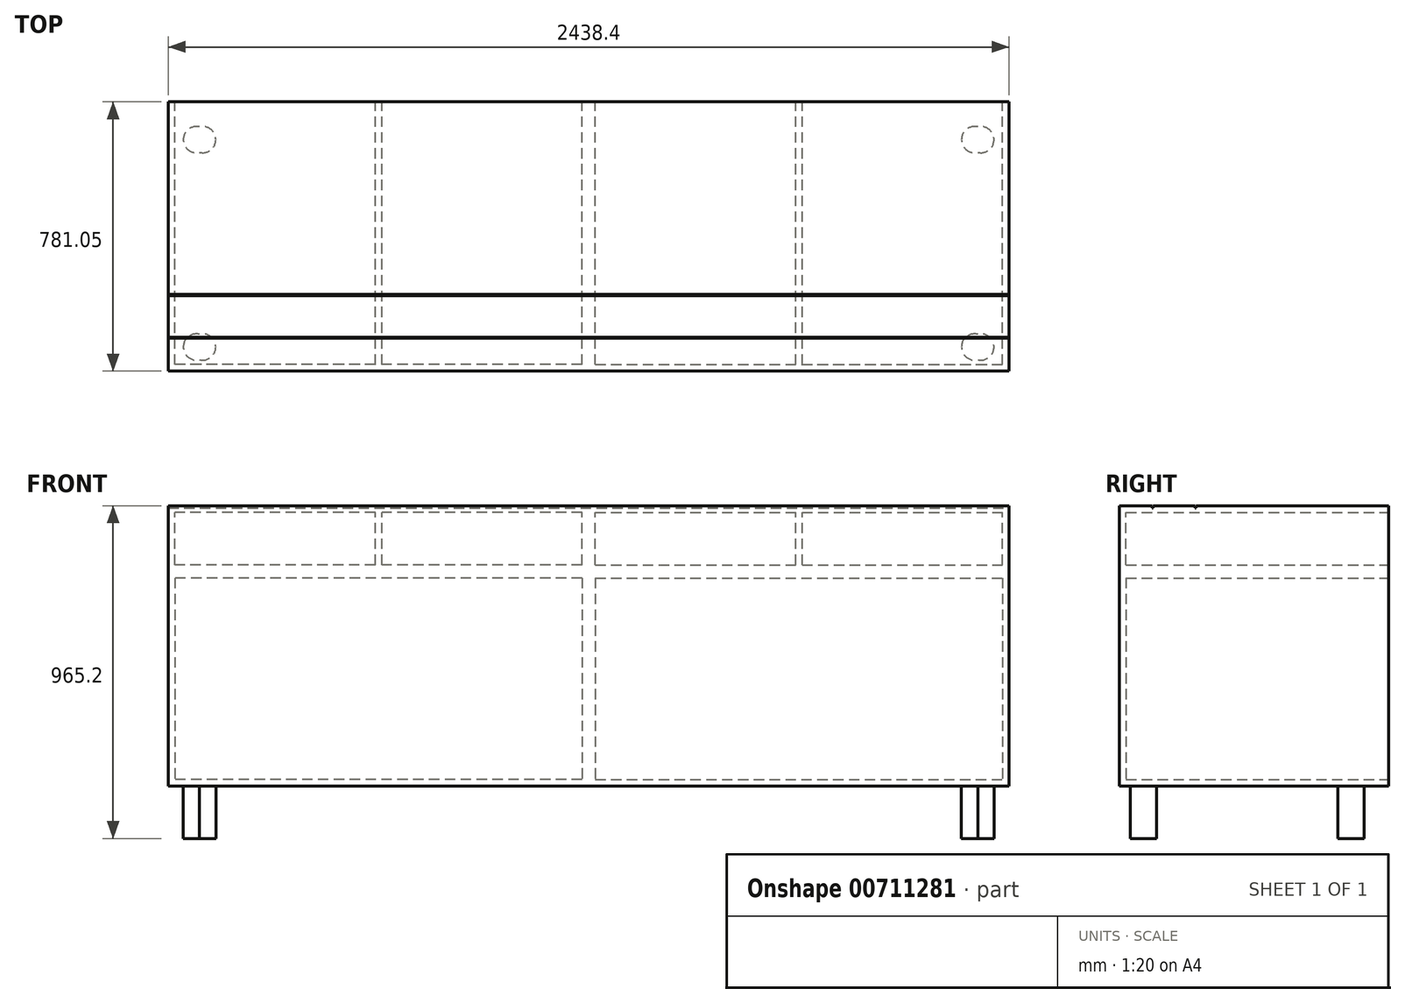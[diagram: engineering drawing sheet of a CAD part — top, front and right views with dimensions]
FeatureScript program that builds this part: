
annotation { "Feature Type Name" : "Feature", "Feature Type Description" : "" }
export const myFeature = defineFeature(function(context is Context, id is Id, definition is map)
    precondition{}
    {
        {
            var Q0;
            Q0=qCreatedBy(makeId("Front.planeOp"),FACE);
            var sketch = newSketch(context, id + "F0", { "sketchPlane" : qUnion([Q0])});
            skLineSegment(sketch, "E0.bottom", {"start": v(0, 0) * mm, "end": v(-1219.2, 0) * mm});
            skLineSegment(sketch, "E0.top", {"start": v(0, 190.5) * mm, "end": v(-1219.2, 190.5) * mm});
            skLineSegment(sketch, "E0.left", {"start": v(0, 0) * mm, "end": v(0, 190.5) * mm});
            skLineSegment(sketch, "E0.right", {"start": v(-1219.2, 0) * mm, "end": v(-1219.2, 190.5) * mm});
            skLineSegment(sketch, "E1.0", {"start": v(-19.05, 171.45) * mm, "end": v(-1200.15, 171.45) * mm});
            skLineSegment(sketch, "E1.1", {"start": v(-19.05, 19.05) * mm, "end": v(-19.05, 171.45) * mm});
            skLineSegment(sketch, "E1.2", {"start": v(-19.05, 19.05) * mm, "end": v(-1200.15, 19.05) * mm});
            skLineSegment(sketch, "E1.3", {"start": v(-1200.15, 19.05) * mm, "end": v(-1200.15, 171.45) * mm});
            skSolve(sketch);
        }
        {
            var Q0;
            Q0 = qSketchRegion(id + "F0", true);
            extrude(context, id + "F1", {"entities" : qUnion([Q0]), "depth" : 762 * mm, "offsetDistance" : 25.4 * mm});
        }
        {
            var Q0;
            Q0=qCreatedBy(makeId("Front.planeOp"),FACE);
            var sketch = newSketch(context, id + "F2", { "sketchPlane" : qUnion([Q0])});
            skLineSegment(sketch, "E2.bottom", {"start": v(0, 0) * mm, "end": v(1219.2, 0) * mm});
            skLineSegment(sketch, "E2.top", {"start": v(0, 190.5) * mm, "end": v(1219.2, 190.5) * mm});
            skLineSegment(sketch, "E2.left", {"start": v(0, 0) * mm, "end": v(0, 190.5) * mm});
            skLineSegment(sketch, "E2.right", {"start": v(1219.2, 0) * mm, "end": v(1219.2, 190.5) * mm});
            skLineSegment(sketch, "E3.0", {"start": v(19.05, 171.45) * mm, "end": v(1200.15, 171.45) * mm});
            skLineSegment(sketch, "E3.1", {"start": v(19.05, 19.05) * mm, "end": v(19.05, 171.45) * mm});
            skLineSegment(sketch, "E3.2", {"start": v(19.05, 19.05) * mm, "end": v(1200.15, 19.05) * mm});
            skLineSegment(sketch, "E3.3", {"start": v(1200.15, 19.05) * mm, "end": v(1200.15, 171.45) * mm});
            skSolve(sketch);
        }
        {
            var Q0;
            Q0=makeQuery(id+"F2.imprint","IMPRINT",FACE,{"disambiguationData":[TD([[makeQuery(id+"F2.imprint","IMPRINT",EDGE,{"derivedFrom":sQuery(id+"F2.wireOp",EDGE,"E2.bottom")}),1.0]])]});
            extrude(context, id + "F3", {"entities" : qUnion([Q0]), "operationType" : NewBodyOperationType.ADD, "depth" : 762 * mm, "offsetDistance" : 25.4 * mm});
        }
        {
            var Q0;
            Q0=qCreatedBy(makeId("Front.planeOp"),FACE);
            var sketch = newSketch(context, id + "F4", { "sketchPlane" : qUnion([Q0])});
            skLineSegment(sketch, "E4.bottom", {"start": v(0, 0) * mm, "end": v(-1219.2, 0) * mm});
            skLineSegment(sketch, "E4.top", {"start": v(0, -622.3) * mm, "end": v(-1219.2, -622.3) * mm});
            skLineSegment(sketch, "E4.left", {"start": v(0, 0) * mm, "end": v(0, -622.3) * mm});
            skLineSegment(sketch, "E4.right", {"start": v(-1219.2, 0) * mm, "end": v(-1219.2, -622.3) * mm});
            skLineSegment(sketch, "E5.0", {"start": v(-19.05, -603.25) * mm, "end": v(-1200.15, -603.25) * mm});
            skLineSegment(sketch, "E5.1", {"start": v(-19.05, -19.05) * mm, "end": v(-19.05, -603.25) * mm});
            skLineSegment(sketch, "E5.2", {"start": v(-19.05, -19.05) * mm, "end": v(-1200.15, -19.05) * mm});
            skLineSegment(sketch, "E5.3", {"start": v(-1200.15, -19.05) * mm, "end": v(-1200.15, -603.25) * mm});
            skLineSegment(sketch, "E6.0", {"start": v(1219.2, 190.5) * mm, "end": v(-1219.2, 190.5) * mm});
            skSolve(sketch);
        }
        {
            var Q0;
            Q0=makeQuery(id+"F4.imprint","IMPRINT",FACE,{"disambiguationData":[TD([[makeQuery(id+"F4.imprint","IMPRINT",EDGE,{"derivedFrom":sQuery(id+"F4.wireOp",EDGE,"E4.bottom")}),1.0]])]});
            extrude(context, id + "F5", {"entities" : qUnion([Q0]), "operationType" : NewBodyOperationType.ADD, "depth" : 762 * mm, "offsetDistance" : 25.4 * mm});
        }
        {
            var Q0;
            Q0=qCreatedBy(makeId("Front.planeOp"),FACE);
            var sketch = newSketch(context, id + "F6", { "sketchPlane" : qUnion([Q0])});
            skLineSegment(sketch, "E7.bottom", {"start": v(0, 0) * mm, "end": v(1219.2, 0) * mm});
            skLineSegment(sketch, "E7.top", {"start": v(0, -622.3) * mm, "end": v(1219.2, -622.3) * mm});
            skLineSegment(sketch, "E7.left", {"start": v(0, 0) * mm, "end": v(0, -622.3) * mm});
            skLineSegment(sketch, "E7.right", {"start": v(1219.2, 0) * mm, "end": v(1219.2, -622.3) * mm});
            skLineSegment(sketch, "E8.0", {"start": v(1219.2, 190.5) * mm, "end": v(-1219.2, 190.5) * mm});
            skLineSegment(sketch, "E9.0", {"start": v(1200.15, -19.05) * mm, "end": v(1200.15, -603.25) * mm});
            skLineSegment(sketch, "E9.1", {"start": v(19.05, -19.05) * mm, "end": v(1200.15, -19.05) * mm});
            skLineSegment(sketch, "E9.2", {"start": v(19.05, -19.05) * mm, "end": v(19.05, -603.25) * mm});
            skLineSegment(sketch, "E9.3", {"start": v(19.05, -603.25) * mm, "end": v(1200.15, -603.25) * mm});
            skSolve(sketch);
        }
        {
            var Q0;
            Q0=makeQuery(id+"F6.imprint","IMPRINT",FACE,{"disambiguationData":[TD([[makeQuery(id+"F6.imprint","IMPRINT",EDGE,{"derivedFrom":sQuery(id+"F6.wireOp",EDGE,"E7.bottom")}),-1.0]])]});
            extrude(context, id + "F7", {"entities" : qUnion([Q0]), "operationType" : NewBodyOperationType.ADD, "depth" : 762 * mm, "offsetDistance" : 25.4 * mm});
        }
        {
            var Q0;
            Q0=makeQuery(id+"F3.boolean.opBoolean","MERGE",FACE,{"derivedFrom":[makeQuery(id+"F1.opExtrude","SWEPT_FACE",FACE,{"disambiguationData":[OSD([sQuery(id+"F0.wireOp",EDGE,"E0.top")])]}),makeQuery(id+"F3.opExtrude","SWEPT_FACE",FACE,{"disambiguationData":[OSD([sQuery(id+"F2.wireOp",EDGE,"E2.top")])]})]});
            var sketch = newSketch(context, id + "F8", { "sketchPlane" : qUnion([Q0])});
            skLineSegment(sketch, "E10.bottom", {"start": v(-1219.2, -685.8) * mm, "end": v(1219.2, -685.8) * mm});
            skLineSegment(sketch, "E10.top", {"start": v(-1219.2, -558.8) * mm, "end": v(1219.2, -558.8) * mm});
            skLineSegment(sketch, "E10.left", {"start": v(-1219.2, -685.8) * mm, "end": v(-1219.2, -558.8) * mm});
            skLineSegment(sketch, "E10.right", {"start": v(1219.2, -685.8) * mm, "end": v(1219.2, -558.8) * mm});
            skSolve(sketch);
        }
        {
            var Q0;
            Q0=makeQuery(id+"F8.imprint","IMPRINT",FACE,{"disambiguationData":[TD([[makeQuery(id+"F8.imprint","IMPRINT",EDGE,{"derivedFrom":sQuery(id+"F8.wireOp",EDGE,"E10.bottom")}),1.0]])]});
            extrude(context, id + "F9", {"entities" : qUnion([Q0]), "operationType" : NewBodyOperationType.REMOVE, "oppositeDirection" : true, "depth" : 6.35 * mm, "offsetDistance" : 25.4 * mm});
        }
        {
            var Q0;
            Q0=makeQuery(id+"F7.boolean.opBoolean","MERGE",FACE,{"derivedFrom":[makeQuery(id+"F5.boolean.opBoolean","MERGE",FACE,{"derivedFrom":[makeQuery(id+"F3.boolean.opBoolean","MERGE",FACE,{"derivedFrom":[makeQuery(id+"F1.opExtrude","CAP_FACE",FACE,{"disambiguationData":[OSD([sQuery(id+"F0.wireOp",EDGE,"E0.bottom"),sQuery(id+"F0.wireOp",EDGE,"E0.top"),sQuery(id+"F0.wireOp",EDGE,"E0.left"),sQuery(id+"F0.wireOp",EDGE,"E0.right"),sQuery(id+"F0.wireOp",EDGE,"E1.0"),sQuery(id+"F0.wireOp",EDGE,"E1.1"),sQuery(id+"F0.wireOp",EDGE,"E1.2"),sQuery(id+"F0.wireOp",EDGE,"E1.3")])],"isStart":false}),makeQuery(id+"F3.opExtrude","CAP_FACE",FACE,{"disambiguationData":[OSD([sQuery(id+"F2.wireOp",EDGE,"E2.bottom"),sQuery(id+"F2.wireOp",EDGE,"E2.top"),sQuery(id+"F2.wireOp",EDGE,"E2.left"),sQuery(id+"F2.wireOp",EDGE,"E2.right"),sQuery(id+"F2.wireOp",EDGE,"E3.0"),sQuery(id+"F2.wireOp",EDGE,"E3.1"),sQuery(id+"F2.wireOp",EDGE,"E3.2"),sQuery(id+"F2.wireOp",EDGE,"E3.3")])],"isStart":false})]}),makeQuery(id+"F5.opExtrude","CAP_FACE",FACE,{"disambiguationData":[OSD([sQuery(id+"F4.wireOp",EDGE,"E4.bottom"),sQuery(id+"F4.wireOp",EDGE,"E4.top"),sQuery(id+"F4.wireOp",EDGE,"E4.left"),sQuery(id+"F4.wireOp",EDGE,"E4.right"),sQuery(id+"F4.wireOp",EDGE,"E5.0"),sQuery(id+"F4.wireOp",EDGE,"E5.1"),sQuery(id+"F4.wireOp",EDGE,"E5.2"),sQuery(id+"F4.wireOp",EDGE,"E5.3")])],"isStart":false})]}),makeQuery(id+"F7.opExtrude","CAP_FACE",FACE,{"disambiguationData":[OSD([sQuery(id+"F6.wireOp",EDGE,"E7.bottom"),sQuery(id+"F6.wireOp",EDGE,"E7.top"),sQuery(id+"F6.wireOp",EDGE,"E7.left"),sQuery(id+"F6.wireOp",EDGE,"E7.right"),sQuery(id+"F6.wireOp",EDGE,"E9.0"),sQuery(id+"F6.wireOp",EDGE,"E9.1"),sQuery(id+"F6.wireOp",EDGE,"E9.2"),sQuery(id+"F6.wireOp",EDGE,"E9.3")])],"isStart":false})]});
            var sketch = newSketch(context, id + "F10", { "sketchPlane" : qUnion([Q0])});
            skLineSegment(sketch, "E11.bottom", {"start": v(-1219.2, -622.3) * mm, "end": v(1219.2, -622.3) * mm});
            skLineSegment(sketch, "E11.top", {"start": v(-1219.2, 190.5) * mm, "end": v(1219.2, 190.5) * mm});
            skLineSegment(sketch, "E11.left", {"start": v(-1219.2, -622.3) * mm, "end": v(-1219.2, 190.5) * mm});
            skLineSegment(sketch, "E11.right", {"start": v(1219.2, -622.3) * mm, "end": v(1219.2, 190.5) * mm});
            skSolve(sketch);
        }
        {
            var Q0;
            Q0 = qSketchRegion(id + "F10", true);
            extrude(context, id + "F11", {"entities" : qUnion([Q0]), "operationType" : NewBodyOperationType.ADD, "depth" : 19.05 * mm, "offsetDistance" : 25.4 * mm});
        }
        {
            var Q0;
            Q0=makeQuery(id+"F11.boolean.opBoolean","MERGE",FACE,{"derivedFrom":[makeQuery(id+"F7.boolean.opBoolean","MERGE",FACE,{"derivedFrom":[makeQuery(id+"F5.opExtrude","SWEPT_FACE",FACE,{"disambiguationData":[OSD([sQuery(id+"F4.wireOp",EDGE,"E4.top")])]}),makeQuery(id+"F7.opExtrude","SWEPT_FACE",FACE,{"disambiguationData":[OSD([sQuery(id+"F6.wireOp",EDGE,"E7.top")])]})]}),makeQuery(id+"F11.opExtrude","SWEPT_FACE",FACE,{"disambiguationData":[OSD([sQuery(id+"F10.wireOp",EDGE,"E11.bottom")])]})]});
            var sketch = newSketch(context, id + "F12", { "sketchPlane" : qUnion([Q0])});
            skCircle(sketch, "E12", {"center": v(1119.46, 109.38) * mm, "radius": 38.1 * mm});
            skLineSegment(sketch, "E13.bottom", {"start": v(1119.46, 109.38) * mm, "end": v(-1137.54, 109.38) * mm, "construction": true});
            skLineSegment(sketch, "E13.top", {"start": v(1119.46, 710.9) * mm, "end": v(-1137.54, 710.9) * mm, "construction": true});
            skLineSegment(sketch, "E13.left", {"start": v(1119.46, 109.38) * mm, "end": v(1119.46, 710.9) * mm, "construction": true});
            skLineSegment(sketch, "E13.right", {"start": v(-1137.54, 109.38) * mm, "end": v(-1137.54, 710.9) * mm, "construction": true});
            skCircle(sketch, "E14", {"center": v(-1137.54, 710.9) * mm, "radius": 38.1 * mm});
            skCircle(sketch, "E15", {"center": v(1119.46, 710.9) * mm, "radius": 38.1 * mm});
            skCircle(sketch, "E16", {"center": v(-1137.54, 109.38) * mm, "radius": 38.1 * mm});
            skSolve(sketch);
        }
        {
            var Q0;
            Q0 = qSketchRegion(id + "F12", true);
            extrude(context, id + "F13", {"entities" : qUnion([Q0]), "operationType" : NewBodyOperationType.ADD, "depth" : 152.4 * mm, "offsetDistance" : 25.4 * mm});
        }
        {
            var Q0;
            Q0=makeQuery(id+"F7.boolean.opBoolean","MERGE",FACE,{"derivedFrom":[makeQuery(id+"F5.boolean.opBoolean","MERGE",FACE,{"derivedFrom":[makeQuery(id+"F3.boolean.opBoolean","MERGE",FACE,{"derivedFrom":[makeQuery(id+"F1.opExtrude","CAP_FACE",FACE,{"disambiguationData":[OSD([sQuery(id+"F0.wireOp",EDGE,"E0.bottom"),sQuery(id+"F0.wireOp",EDGE,"E0.top"),sQuery(id+"F0.wireOp",EDGE,"E0.left"),sQuery(id+"F0.wireOp",EDGE,"E0.right"),sQuery(id+"F0.wireOp",EDGE,"E1.0"),sQuery(id+"F0.wireOp",EDGE,"E1.1"),sQuery(id+"F0.wireOp",EDGE,"E1.2"),sQuery(id+"F0.wireOp",EDGE,"E1.3")])],"isStart":true}),makeQuery(id+"F3.opExtrude","CAP_FACE",FACE,{"disambiguationData":[OSD([sQuery(id+"F2.wireOp",EDGE,"E2.bottom"),sQuery(id+"F2.wireOp",EDGE,"E2.top"),sQuery(id+"F2.wireOp",EDGE,"E2.left"),sQuery(id+"F2.wireOp",EDGE,"E2.right"),sQuery(id+"F2.wireOp",EDGE,"E3.0"),sQuery(id+"F2.wireOp",EDGE,"E3.1"),sQuery(id+"F2.wireOp",EDGE,"E3.2"),sQuery(id+"F2.wireOp",EDGE,"E3.3")])],"isStart":true})]}),makeQuery(id+"F5.opExtrude","CAP_FACE",FACE,{"disambiguationData":[OSD([sQuery(id+"F4.wireOp",EDGE,"E4.bottom"),sQuery(id+"F4.wireOp",EDGE,"E4.top"),sQuery(id+"F4.wireOp",EDGE,"E4.left"),sQuery(id+"F4.wireOp",EDGE,"E4.right"),sQuery(id+"F4.wireOp",EDGE,"E5.0"),sQuery(id+"F4.wireOp",EDGE,"E5.1"),sQuery(id+"F4.wireOp",EDGE,"E5.2"),sQuery(id+"F4.wireOp",EDGE,"E5.3")])],"isStart":true})]}),makeQuery(id+"F7.opExtrude","CAP_FACE",FACE,{"disambiguationData":[OSD([sQuery(id+"F6.wireOp",EDGE,"E7.bottom"),sQuery(id+"F6.wireOp",EDGE,"E7.top"),sQuery(id+"F6.wireOp",EDGE,"E7.left"),sQuery(id+"F6.wireOp",EDGE,"E7.right"),sQuery(id+"F6.wireOp",EDGE,"E9.0"),sQuery(id+"F6.wireOp",EDGE,"E9.1"),sQuery(id+"F6.wireOp",EDGE,"E9.2"),sQuery(id+"F6.wireOp",EDGE,"E9.3")])],"isStart":true})]});
            var sketch = newSketch(context, id + "F14", { "sketchPlane" : qUnion([Q0])});
            skLineSegment(sketch, "E17.0", {"start": v(-19.05, 19.05) * mm, "end": v(-1200.15, 19.05) * mm, "construction": true});
            skLineSegment(sketch, "E17.1", {"start": v(-19.05, 171.45) * mm, "end": v(-1200.15, 171.45) * mm, "construction": true});
            skLineSegment(sketch, "E18.bottom", {"start": v(-600.07, 19.05) * mm, "end": v(-619.12, 19.05) * mm});
            skLineSegment(sketch, "E18.top", {"start": v(-600.07, 171.45) * mm, "end": v(-619.12, 171.45) * mm});
            skLineSegment(sketch, "E18.left", {"start": v(-600.07, 19.05) * mm, "end": v(-600.07, 171.45) * mm});
            skLineSegment(sketch, "E18.right", {"start": v(-619.12, 19.05) * mm, "end": v(-619.12, 171.45) * mm});
            skPoint(sketch, "E19", {"position": v(-609.6, 19.05) * mm});
            skSolve(sketch);
        }
        {
            var Q0;
            Q0 = qSketchRegion(id + "F14", true);
            extrude(context, id + "F15", {"entities" : qUnion([Q0]), "operationType" : NewBodyOperationType.ADD, "endBound" : BoundingType.UP_TO_NEXT, "oppositeDirection" : true, "depth" : 25.4 * mm, "offsetDistance" : 25.4 * mm});
        }
        {
            var Q0;
            Q0=makeQuery(id+"F1.opExtrude","SWEPT_BODY",BODY,{"disambiguationData":[OSD([sQuery(id+"F0.wireOp",EDGE,"E0.bottom"),sQuery(id+"F0.wireOp",EDGE,"E0.top"),sQuery(id+"F0.wireOp",EDGE,"E0.left"),sQuery(id+"F0.wireOp",EDGE,"E0.right"),sQuery(id+"F0.wireOp",EDGE,"E1.0"),sQuery(id+"F0.wireOp",EDGE,"E1.1"),sQuery(id+"F0.wireOp",EDGE,"E1.2"),sQuery(id+"F0.wireOp",EDGE,"E1.3")])]});
            var Q1;
            Q1=qCreatedBy(makeId("Right.planeOp"),FACE);
            mirror(context, id + "F16", {"operationType" : NewBodyOperationType.ADD, "entities" : qUnion([Q0]), "mirrorPlane" : qUnion([Q1])});
        }
        {
            var Q0;
            Q0=makeQuery(id+"F11.boolean.opBoolean","MERGE",FACE,{"derivedFrom":[makeQuery(id+"F7.boolean.opBoolean","MERGE",FACE,{"derivedFrom":[makeQuery(id+"F3.opExtrude","SWEPT_FACE",FACE,{"disambiguationData":[OSD([sQuery(id+"F2.wireOp",EDGE,"E2.right")])]}),makeQuery(id+"F7.opExtrude","SWEPT_FACE",FACE,{"disambiguationData":[OSD([sQuery(id+"F6.wireOp",EDGE,"E7.right")])]})]}),makeQuery(id+"F11.opExtrude","SWEPT_FACE",FACE,{"disambiguationData":[OSD([sQuery(id+"F10.wireOp",EDGE,"E11.right")])]})]});
            var sketch = newSketch(context, id + "F17", { "sketchPlane" : qUnion([Q0])});
            skLineSegment(sketch, "E20.bottom", {"start": v(-683.12, 184.15) * mm, "end": v(-561.67, 184.15) * mm});
            skLineSegment(sketch, "E20.top", {"start": v(-683.12, 190.5) * mm, "end": v(-561.67, 190.5) * mm});
            skLineSegment(sketch, "E20.left", {"start": v(-683.12, 184.15) * mm, "end": v(-683.12, 190.5) * mm});
            skLineSegment(sketch, "E20.right", {"start": v(-561.67, 184.15) * mm, "end": v(-561.67, 190.5) * mm});
            skSolve(sketch);
        }
        {
            var Q0;
            Q0 = qSketchRegion(id + "F17", true);
            var Q1;
            Q1=makeQuery(id+"F11.boolean.opBoolean","MERGE",FACE,{"derivedFrom":[makeQuery(id+"F5.boolean.opBoolean","MERGE",FACE,{"derivedFrom":[makeQuery(id+"F1.opExtrude","SWEPT_FACE",FACE,{"disambiguationData":[OSD([sQuery(id+"F0.wireOp",EDGE,"E0.right")])]}),makeQuery(id+"F5.opExtrude","SWEPT_FACE",FACE,{"disambiguationData":[OSD([sQuery(id+"F4.wireOp",EDGE,"E4.right")])]})]}),makeQuery(id+"F11.opExtrude","SWEPT_FACE",FACE,{"disambiguationData":[OSD([sQuery(id+"F10.wireOp",EDGE,"E11.left")])]})]});
            extrude(context, id + "F18", {"entities" : qUnion([Q0]), "operationType" : NewBodyOperationType.ADD, "endBound" : BoundingType.UP_TO_SURFACE, "oppositeDirection" : true, "depth" : 25.4 * mm, "endBoundEntityFace" : qUnion([Q1]), "offsetDistance" : 25.4 * mm});
        }
    });
